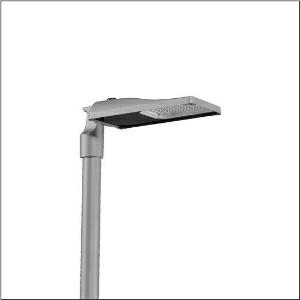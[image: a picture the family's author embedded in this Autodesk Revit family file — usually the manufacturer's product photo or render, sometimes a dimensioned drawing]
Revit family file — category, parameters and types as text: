
# Revit family: streetlight_sl_31_mini___st1_0a_5xh2d31s08ja_14e0
name_source: partatom
category: Lighting Fixtures
units: mm (PartAtom-declared; Revit-internal decimal feet)

## family parameters
Cut with Voids When Loaded = No
Host = Face
Light Source = No
Part Type = Normal
Room Calculation Point = No
Round Connector Dimension = Use Diameter
Shared = No

## types (1)
- --- (1 x LED, 12270 lm, 82.5 W, 3000K)
    Apparent Load = 83 VA
    CIE Flux Codes = 40 73 97 100 100
    Color Rendering = 70
    Color Temperature = 3000K
    Default Elevation = 1800 mm
    Description = Streetlight SL 31 mini D4i, Desk-Remote mast luminaire for post-top, side-entry; light control with lens of PMMA; light distribution: ST1.0a, direct asymmetric distribution, for standard-compliant lighting for roads and squares; LED: luminous flux: 12.270lm, light colour: 730, colour temperature: 3000K; luminous efficacy: 148,7lm/W; control: pre-setting: logarithmic dimming characteristic, flexible luminous flux parameterisation, time-dependent luminous flux control, constant luminous flux control, power reduction, intelligent temperature release in ECG and LED module, overheat protection; luminaire housing, of diecast aluminium, Siteco® metallic grey (DB 702S), corrosivity category C5 high according to DIN EN ISO 12944; cover of toughened safety glass, transparent, mast flange of diecast aluminium, Siteco® metallic grey (DB 702S), spigot size: 76/60mm, mast flange included unmounted; with cable H07RN-F 2x 1.5mm², cable length: 10,5m, connection cable pre-assembled; mains connection: 220..240V, AC, 50/60Hz; power consumption (at start of service life): 82,5W / (at end of service life): 90,1W / (with reduced operation 50%): 36,8W; protection rating (complete): IP66; insulation class (complete): insulation class II (safety insulation); impact resistance: IK10; certification: CE, ENEC, ENEC+, VDE, UKCA, ZD4i; permissible operating ambient temperature for outdoor applications: -40..+50°C; packaging unit: 1 piece

Light Distribution: ST1.0a
    Height = 76 mm
    Lamp = 1 x LED
    Lamp Light Flux = 12270 lm
    Lamp Power = 82.5 W
    Lamp count = 1
    Length = 547 mm
    Luminous efficacy = 149 lm/W
    Manufacturer = Siteco
    ModVariant = No
    Model = 5XH2D31S08JA
    Number of Poles = 1
    OnlyDefault = Yes
    Power Factor = 1
    Product Name = Streetlight SL 31 mini | ST1.0a
    Product group = mast luminaire | pylon top
    ProductGroupID = 6100
    Protection Class = Protection class II
    Protection Degree = IP 66
    RLX_Detail_Level = 1
    RLX_Emergency_Light_Flux = 0 lm
    RLX_Emergency_Type = 0
    RLX_Emergency_Type_DB = No
    RlxData = <blob elided: 39785 chars, md5=badb0067>
    Socket = socket
    Standby Power = 0 W
    System Light Flux = 12270 lm
    System Power = 83 W
    Type Comments = factory setting: luminous flux: 100 % | dim-lin: 254 | 870 mA
    Type Image = l_1300330.jpg
    URL = http://relux.com
    VarID = @adj_071397
    Voltage = 0 V
    Weight = 0.00 kg
    Width = 265 mm

## geometry (parser evidence)
native form markers: Blend x4, Sweep x11
no freeform markers — native parametric forms only
